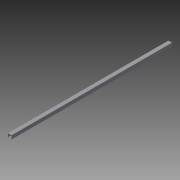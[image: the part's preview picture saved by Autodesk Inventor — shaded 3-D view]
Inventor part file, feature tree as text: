
AUTODESK INVENTOR PART (.ipt)
format: ipt  version: 2013 (Build 170138000, 138)  size: 75,264 bytes
history: native  units: in
note: dims shown in document units (in); Inventor stores cm internally (conversion verified against a paired STEP export)
features: extrude x1, sketch x1
ambient origin geometry x8: Origin, YZ Plane, XZ Plane, XY Plane, X Axis, Y Axis, Z Axis, Center Point
bodies: Solid1 (feature_tree)
feature tree (2):
  extrude  "Extrusion1"  Depth=1.75in
  sketch  "Sketch1"  dims[d0=1.75in d1=1.75in d2=0.125in d3=78.0in d4=0.0in]
